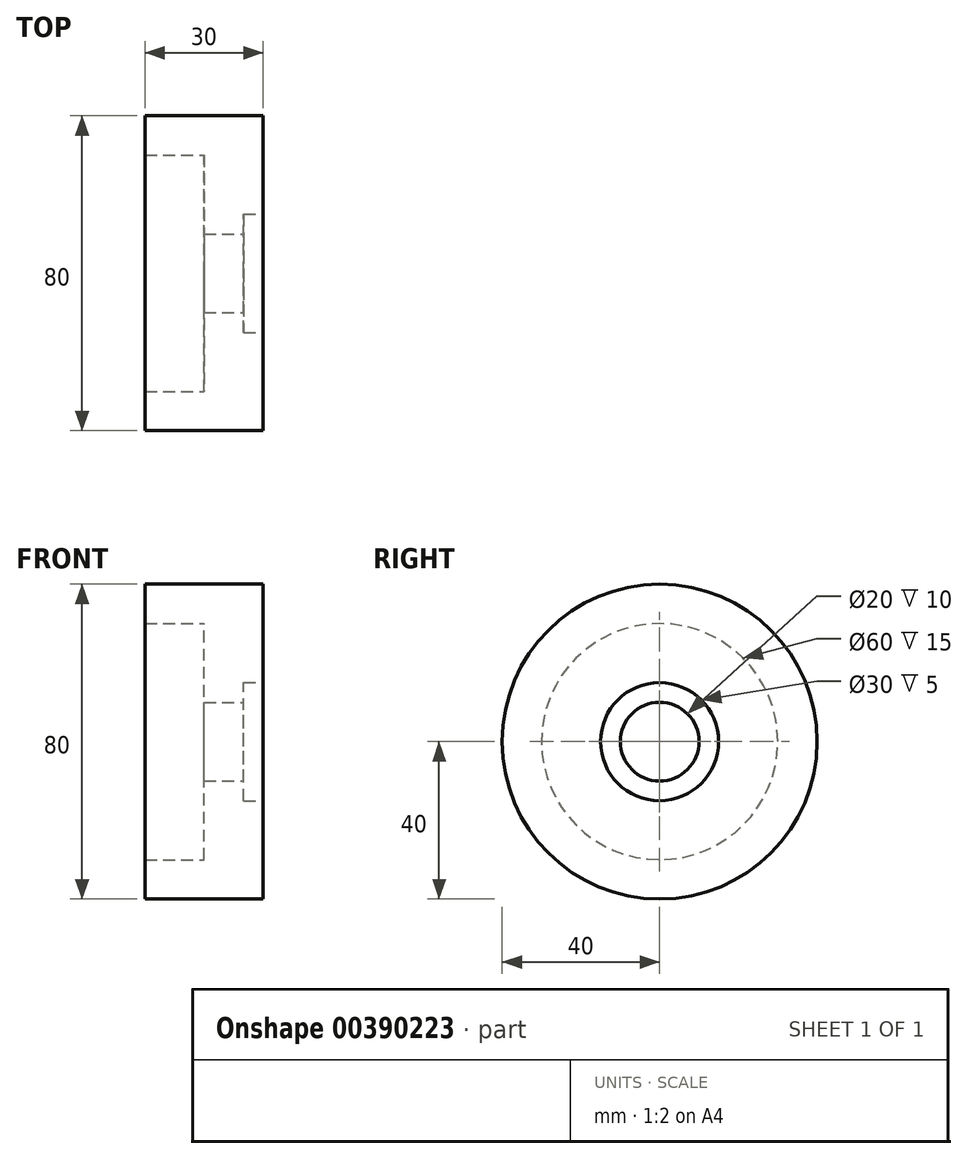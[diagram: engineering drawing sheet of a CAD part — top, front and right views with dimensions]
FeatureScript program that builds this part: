
annotation { "Feature Type Name" : "Feature", "Feature Type Description" : "" }
export const myFeature = defineFeature(function(context is Context, id is Id, definition is map)
    precondition{}
    {
        {
            var Q0;
            Q0=qCreatedBy(makeId("Front.planeOp"),FACE);
            var sketch = newSketch(context, id + "F0", { "sketchPlane" : qUnion([Q0])});
            skLineSegment(sketch, "E0", {"start": v(-7.5, 0) * mm, "end": v(-7.5, -30) * mm});
            skLineSegment(sketch, "E1", {"start": v(-7.5, -30) * mm, "end": v(-22.5, -30) * mm});
            skLineSegment(sketch, "E2", {"start": v(-22.5, -30) * mm, "end": v(-22.5, -40) * mm});
            skLineSegment(sketch, "E3", {"start": v(-22.5, -40) * mm, "end": v(7.5, -40) * mm});
            skLineSegment(sketch, "E4", {"start": v(7.5, -40) * mm, "end": v(7.5, 0) * mm});
            skLineSegment(sketch, "E5", {"start": v(7.5, 0) * mm, "end": v(-7.5, 0) * mm});
            skPoint(sketch, "E6.endSnap0", {"position": v(0, 0) * mm});
            skSolve(sketch);
        }
        {
            var Q0;
            Q0=makeQuery(id+"F0.imprint","IMPRINT",FACE,{"disambiguationData":[TD([[makeQuery(id+"F0.imprint","IMPRINT",EDGE,{"derivedFrom":sQuery(id+"F0.wireOp",EDGE,"E0")}),1.0]])]});
            var Q1;
            Q1=sQuery(id+"F0.wireOp",EDGE,"E5");
            revolve(context, id + "F1", {"entities" : qUnion([Q0]), "axis" : qUnion([Q1]), "revolveType" : RevolveType.FULL});
        }
        {
            var Q0;
            Q0=makeQuery(id+"F1.opRevolve","SWEPT_FACE",FACE,{"disambiguationData":[OSD([sQuery(id+"F0.wireOp",EDGE,"E4")])]});
            var sketch = newSketch(context, id + "F2", { "sketchPlane" : qUnion([Q0])});
            skCircle(sketch, "E7", {"center": v(0, 0) * mm, "radius": 15 * mm});
            skCircle(sketch, "E8", {"center": v(0, 0) * mm, "radius": 10 * mm});
            skSolve(sketch);
        }
        {
            var Q0;
            Q0=makeQuery(id+"F2.imprint","IMPRINT",FACE,{"disambiguationData":[TD([[makeQuery(id+"F2.imprint","IMPRINT",EDGE,{"derivedFrom":sQuery(id+"F2.wireOp",EDGE,"E8")}),1.0]])]});
            extrude(context, id + "F3", {"entities" : qUnion([Q0]), "operationType" : NewBodyOperationType.REMOVE, "oppositeDirection" : true, "depth" : 25 * mm});
        }
        {
            var Q0;
            Q0=makeQuery(id+"F2.imprint","IMPRINT",FACE,{"disambiguationData":[TD([[makeQuery(id+"F2.imprint","IMPRINT",EDGE,{"derivedFrom":sQuery(id+"F2.wireOp",EDGE,"E7")}),1.0]])]});
            extrude(context, id + "F4", {"entities" : qUnion([Q0]), "operationType" : NewBodyOperationType.REMOVE, "oppositeDirection" : true, "depth" : 5 * mm});
        }
    });
